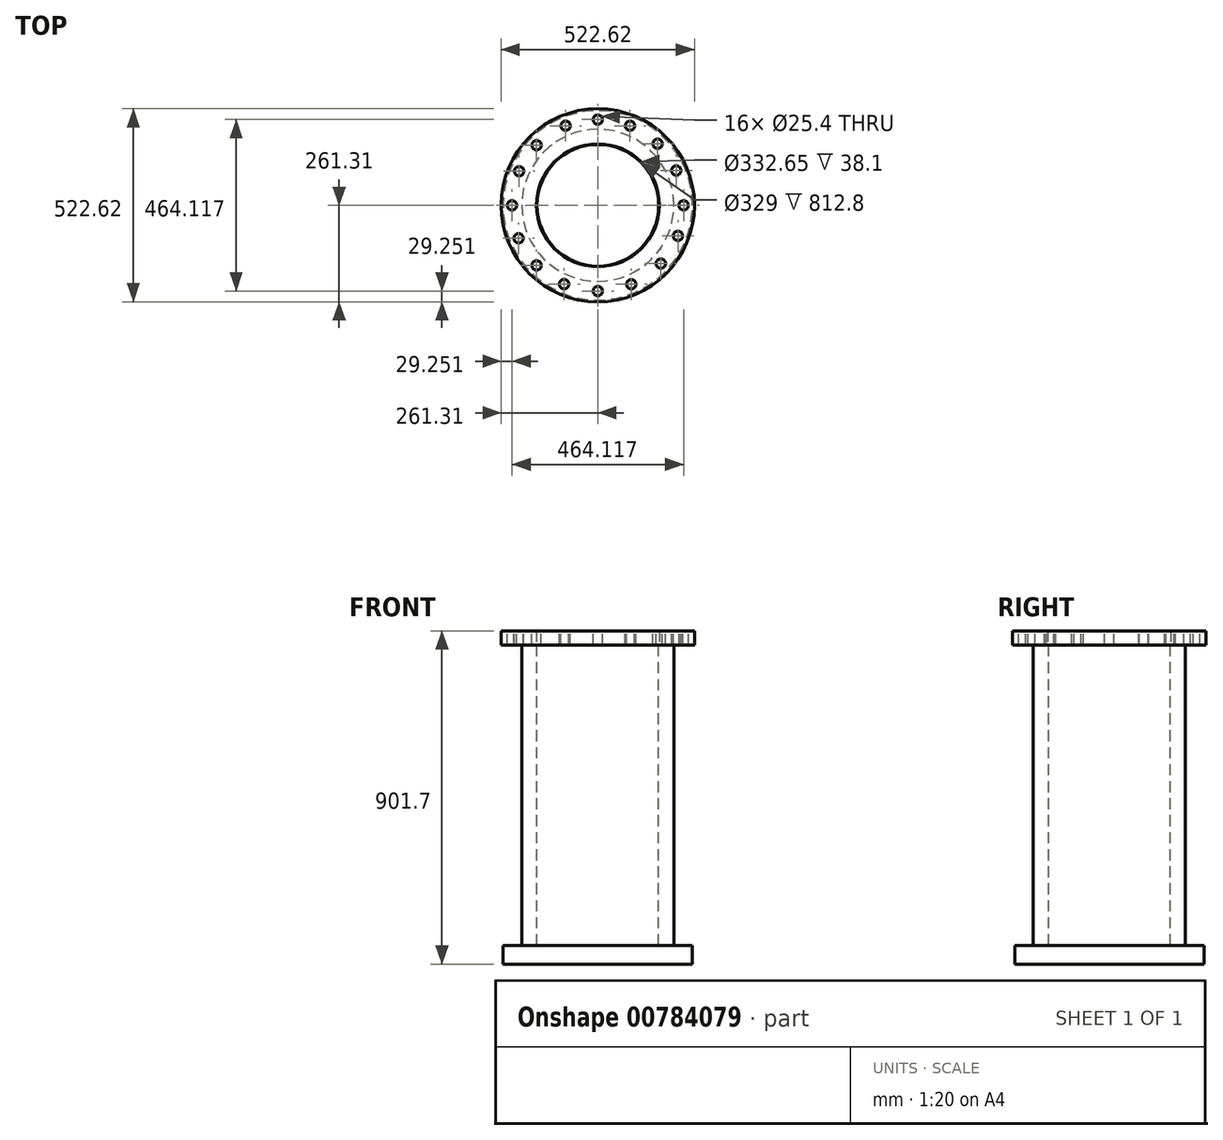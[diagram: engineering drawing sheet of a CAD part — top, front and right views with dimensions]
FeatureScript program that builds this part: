
annotation { "Feature Type Name" : "Feature", "Feature Type Description" : "" }
export const myFeature = defineFeature(function(context is Context, id is Id, definition is map)
    precondition{}
    {
        {
            var Q0;
            Q0=qCreatedBy(makeId("Top.planeOp"),FACE);
            var sketch = newSketch(context, id + "F0", { "sketchPlane" : qUnion([Q0])});
            skCircle(sketch, "E0", {"center": v(0, 0) * mm, "radius": 164.5 * mm});
            skCircle(sketch, "E1", {"center": v(0, 0) * mm, "radius": 205.63 * mm});
            skSolve(sketch);
        }
        {
            var Q0;
            Q0=makeQuery(id+"F0.imprint","IMPRINT",FACE,{"disambiguationData":[TD([[makeQuery(id+"F0.imprint","IMPRINT",EDGE,{"derivedFrom":sQuery(id+"F0.wireOp",EDGE,"E0")}),-1.0]])]});
            extrude(context, id + "F1", {"entities" : qUnion([Q0]), "oppositeDirection" : true, "depth" : 812.8 * mm, "offsetDistance" : 25.4 * mm});
        }
        {
            var Q0;
            Q0=makeQuery(id+"F1.opExtrude","CAP_FACE",FACE,{"disambiguationData":[OSD([sQuery(id+"F0.wireOp",EDGE,"E0"),sQuery(id+"F0.wireOp",EDGE,"E1")])],"isStart":false});
            var sketch = newSketch(context, id + "F2", { "sketchPlane" : qUnion([Q0])});
            skCircle(sketch, "E2", {"center": v(0, 0) * mm, "radius": 256 * mm});
            skSolve(sketch);
        }
        {
            var Q0;
            Q0 = qSketchRegion(id + "F2", true);
            extrude(context, id + "F3", {"entities" : qUnion([Q0]), "operationType" : NewBodyOperationType.ADD, "depth" : 50.8 * mm, "offsetDistance" : 25.4 * mm});
        }
        {
            var Q0;
            Q0=makeQuery(id+"F1.opExtrude","CAP_FACE",FACE,{"disambiguationData":[OSD([sQuery(id+"F0.wireOp",EDGE,"E0"),sQuery(id+"F0.wireOp",EDGE,"E1")])],"isStart":true});
            var sketch = newSketch(context, id + "F4", { "sketchPlane" : qUnion([Q0])});
            skCircle(sketch, "E3", {"center": v(0, 0) * mm, "radius": 261.3 * mm});
            skCircle(sketch, "E4", {"center": v(0, 0) * mm, "radius": 166.33 * mm});
            skCircle(sketch, "E5", {"center": v(0, 0) * mm, "radius": 231.5 * mm, "construction": true});
            skSolve(sketch);
        }
        {
            var Q0;
            Q0 = qSketchRegion(id + "F4", true);
            extrude(context, id + "F5", {"entities" : qUnion([Q0]), "operationType" : NewBodyOperationType.ADD, "depth" : 38.1 * mm, "offsetDistance" : 25.4 * mm});
        }
        {
            var Q0;
            Q0=makeQuery(id+"F5.opExtrude","CAP_FACE",FACE,{"disambiguationData":[OSD([sQuery(id+"F4.wireOp",EDGE,"E3"),sQuery(id+"F4.wireOp",EDGE,"E4"),sQuery(id+"F4.wireOp",EDGE,"TsgfCbS9-atlK-9YMo-gimO-ki3xV197YjQp")])],"isStart":false});
            var sketch = newSketch(context, id + "F6", { "sketchPlane" : qUnion([Q0])});
            skCircle(sketch, "E6", {"center": v(0, 0) * mm, "radius": 232.06 * mm, "construction": true});
            skPoint(sketch, "E7", {"position": v(-232.06, 0) * mm});
            skPoint(sketch, "E8", {"position": v(232.06, 0) * mm});
            skPoint(sketch, "E9", {"position": v(0, 232.06) * mm});
            skPoint(sketch, "E10", {"position": v(0, -232.06) * mm});
            skPoint(sketch, "E11", {"position": v(161.68, 166.47) * mm});
            skPoint(sketch, "E12", {"position": v(-165.6, 162.57) * mm});
            skPoint(sketch, "E13", {"position": v(170.39, -157.54) * mm});
            skPoint(sketch, "E14", {"position": v(-165.6, -162.57) * mm});
            skPoint(sketch, "E15", {"position": v(87.06, 215.1) * mm});
            skPoint(sketch, "E16", {"position": v(212.17, 94) * mm});
            skPoint(sketch, "E17", {"position": v(216.82, -82.71) * mm});
            skPoint(sketch, "E18", {"position": v(90.52, -213.67) * mm});
            skPoint(sketch, "E19", {"position": v(-91.3, -213.35) * mm});
            skPoint(sketch, "E20", {"position": v(-214.24, -89.17) * mm});
            skPoint(sketch, "E21", {"position": v(-212.9, 92.34) * mm});
            skPoint(sketch, "E22", {"position": v(-87.06, 215.1) * mm});
            skSolve(sketch);
        }
        {
            var Q0;
            Q0=sQuery(id+"F6.wireOp",VERTEX,"E15");
            var Q1;
            Q1=sQuery(id+"F6.wireOp",VERTEX,"E11");
            var Q2;
            Q2=sQuery(id+"F6.wireOp",VERTEX,"E16");
            var Q3;
            Q3=sQuery(id+"F6.wireOp",VERTEX,"E8");
            var Q4;
            Q4=sQuery(id+"F6.wireOp",VERTEX,"E17");
            var Q5;
            Q5=sQuery(id+"F6.wireOp",VERTEX,"E13");
            var Q6;
            Q6=sQuery(id+"F6.wireOp",VERTEX,"E18");
            var Q7;
            Q7=sQuery(id+"F6.wireOp",VERTEX,"E10");
            var Q8;
            Q8=sQuery(id+"F6.wireOp",VERTEX,"E19");
            var Q9;
            Q9=sQuery(id+"F6.wireOp",VERTEX,"E14");
            var Q10;
            Q10=sQuery(id+"F6.wireOp",VERTEX,"E20");
            var Q11;
            Q11=sQuery(id+"F6.wireOp",VERTEX,"E7");
            var Q12;
            Q12=sQuery(id+"F6.wireOp",VERTEX,"E21");
            var Q13;
            Q13=sQuery(id+"F6.wireOp",VERTEX,"E12");
            var Q14;
            Q14=sQuery(id+"F6.wireOp",VERTEX,"E22");
            var Q15;
            Q15=sQuery(id+"F6.wireOp",VERTEX,"E9");
            var Q16;
            Q16=makeQuery(id+"F1.opExtrude","SWEPT_BODY",BODY,{"disambiguationData":[OSD([sQuery(id+"F0.wireOp",EDGE,"E0"),sQuery(id+"F0.wireOp",EDGE,"E1")])]});
            hole(context, id + "F7", {"style" : HoleStyle.SIMPLE, "endStyle" : HoleEndStyle.BLIND, "holeDiameter" : 25.4 * mm, "majorDiameter" : 6.35 * mm, "holeDepth" : 50.8 * mm, "isTappedThrough" : true, "tappedDepth" : 12.7 * mm, "tapClearance" : 3, "locations" : qUnion([Q0, Q1, Q2, Q3, Q4, Q5, Q6, Q7, Q8, Q9, Q10, Q11, Q12, Q13, Q14, Q15]), "scope" : qUnion([Q16])});
        }
    });
